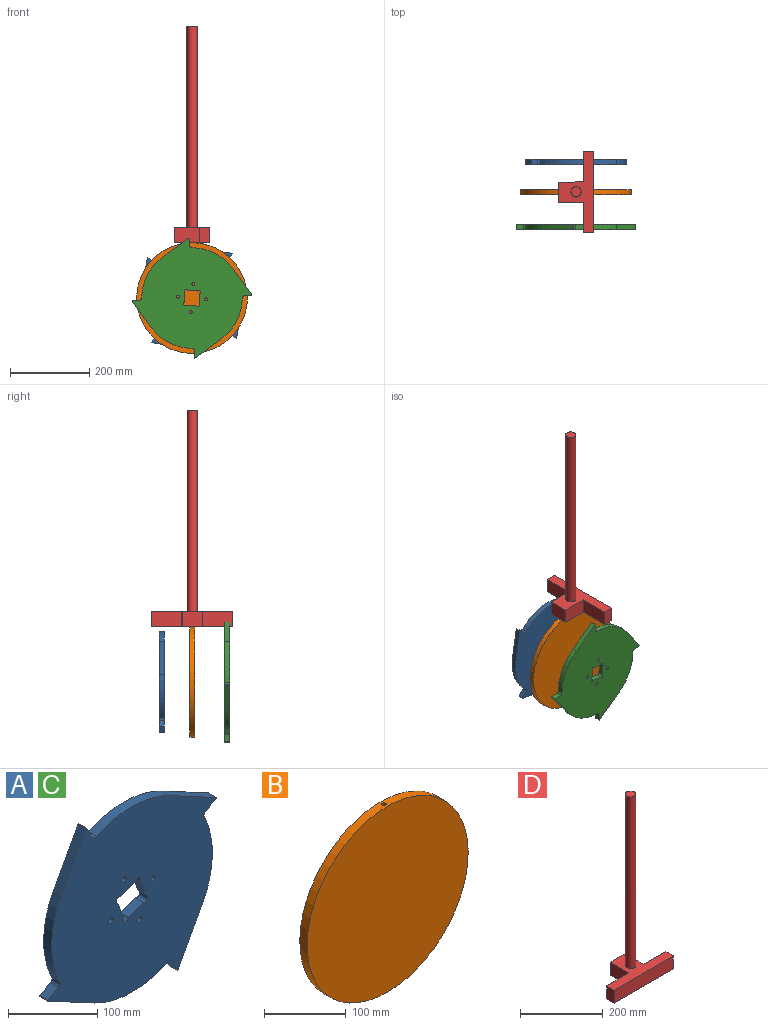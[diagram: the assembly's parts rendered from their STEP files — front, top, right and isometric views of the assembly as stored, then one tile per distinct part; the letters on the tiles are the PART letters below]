
ASSEMBLY  parts=4 mates=3
PART A: 34 faces, bbox 266.9x12.7x266.9 mm
  f0: plane 266.87x266.87mm, normal (0,-1,0), area 51514.2mm2, adj f2,f3,f4,f5,f6,f7,f8,f9
  f1: plane 266.87x266.87mm, normal (0,1,0), area 51514.2mm2, adj f2,f3,f4,f5,f6,f7,f8,f9
  f2: cylinder r=127mm len=115.76mm, axis (0,1,0), area 1526.8mm2, adj f0,f1,f13,f26
  f3: plane 16.74x12.7mm, normal (-0.47,0,0.88), area 241.3mm2, adj f0,f1,f26,f30
  f4: plane 72.98x39.17mm, normal (-0.47,0,-0.88), area 1051.8mm2, adj f0,f1,f5,f30
  f5: cylinder r=127mm len=115.76mm, axis (0,1,0), area 1526.8mm2, adj f0,f1,f4,f27
  f6: plane 16.74x12.7mm, normal (-0.88,0,-0.47), area 241.3mm2, adj f0,f1,f27,f31
  f7: plane 72.98x39.17mm, normal (0.88,0,-0.47), area 1051.8mm2, adj f0,f1,f8,f31
  f8: cylinder r=127mm len=115.76mm, axis (0,1,0), area 1526.8mm2, adj f0,f1,f7,f28
  f9: plane 16.74x12.7mm, normal (0.47,0,-0.88), area 241.3mm2, adj f0,f1,f28,f32
  f10: plane 72.98x39.17mm, normal (0.47,0,0.88), area 1051.8mm2, adj f0,f1,f11,f32
  f11: cylinder r=127mm len=115.76mm, axis (0,1,0), area 1526.8mm2, adj f0,f1,f10,f29
  f12: plane 16.74x12.7mm, normal (0.88,0,0.47), area 241.3mm2, adj f0,f1,f29,f33
  f13: plane 72.98x39.17mm, normal (-0.88,0,0.47), area 1051.8mm2, adj f0,f1,f2,f33
  f14: cylinder r=3.81mm len=12.7mm, axis (0,-1,0), area 304mm2, adj f0,f1
  f15: cylinder r=3.81mm len=12.7mm, axis (0,-1,0), area 304mm2, adj f0,f1
  f16: cylinder r=3.81mm len=12.7mm, axis (0,-1,0), area 304mm2, adj f0,f1
  f17: cylinder r=4.49mm len=12.7mm, axis (0,-1,0), area 179.1mm2, adj f0,f1,f18,f24
  f18: plane 23.87x12.7mm, normal (0.94,0,0.34), area 322.6mm2, adj f0,f1,f17,f19
  f19: cylinder r=4.49mm len=12.7mm, axis (0,-1,0), area 179.1mm2, adj f0,f1,f18,f20
  f20: plane 23.87x12.7mm, normal (-0.34,0,0.94), area 322.6mm2, adj f0,f1,f19,f21
  f21: cylinder r=4.49mm len=12.7mm, axis (0,-1,0), area 179.1mm2, adj f0,f1,f20,f22
  f22: plane 23.87x12.7mm, normal (-0.94,0,-0.34), area 322.6mm2, adj f0,f1,f21,f23
  f23: cylinder r=4.49mm len=12.7mm, axis (0,-1,0), area 179.1mm2, adj f0,f1,f22,f24
  f24: plane 23.87x12.7mm, normal (0.34,0,-0.94), area 322.6mm2, adj f0,f1,f17,f23
  f25: cylinder r=3.81mm len=12.7mm, axis (0,-1,0), area 304mm2, adj f0,f1
  f26: cylinder r=5.08mm len=12.7mm, axis (0,1,0), area 98.9mm2, adj f0,f1,f2,f3
  f27: cylinder r=5.08mm len=12.7mm, axis (0,1,0), area 98.9mm2, adj f0,f1,f5,f6
  f28: cylinder r=5.08mm len=12.7mm, axis (0,1,0), area 98.9mm2, adj f0,f1,f8,f9
  f29: cylinder r=5.08mm len=12.7mm, axis (0,1,0), area 98.9mm2, adj f0,f1,f11,f12
  f30: cylinder r=0.76mm len=12.7mm, axis (0,1,0), area 20.9mm2, adj f0,f1,f3,f4
  f31: cylinder r=0.76mm len=12.7mm, axis (0,1,0), area 20.9mm2, adj f0,f1,f6,f7
  f32: cylinder r=0.76mm len=12.7mm, axis (0,-1,0), area 20.9mm2, adj f0,f1,f9,f10
  f33: cylinder r=0.76mm len=12.7mm, axis (0,1,0), area 20.9mm2, adj f0,f1,f12,f13
PART B: 4 faces, bbox 279.4x12.7x279.4 mm
  f0: cylinder r=139.7mm len=279.4mm, axis (0,1,0), area 11106.9mm2, adj f1,f2,f3
  f1: plane 279.4x279.4mm, normal (0,-1,0), area 61311.6mm2, adj f0
  f2: plane 279.4x279.4mm, normal (0,1,0), area 61311.6mm2, adj f0
  f3: cylinder r=2.54mm len=279.4mm, axis (0,0,-1), area 4458.7mm2, adj f0
PART C: same geometry as A
PART D: 12 faces, bbox 203.2x88.9x546.1 mm
  f0: plane 50.8x38.1mm, normal (0,1,0), area 1935.5mm2, adj f6,f7,f8,f11
  f1: plane 38.1x25.4mm, normal (1,0,0), area 967.7mm2, adj f5,f6,f7,f9
  f2: plane 38.1x25.4mm, normal (-1,0,0), area 967.7mm2, adj f5,f6,f7,f10
  f3: cylinder r=12.7mm len=508mm, axis (0,0,-1), area 40536.6mm2, adj f4,f7
  f4: plane 25.4x25.4mm, normal (0,0,1), area 506.7mm2, adj f3
  f5: plane 203.2x38.1mm, normal (0,-1,0), area 7741.9mm2, adj f1,f2,f6,f7
  f6: plane 203.2x88.9mm, normal (0,0,-1), area 8387.1mm2, adj f0,f1,f2,f5,f8,f9,f10,f11
  f7: plane 203.2x88.9mm, normal (0,0,1), area 7880.4mm2, adj f0,f1,f2,f3,f5,f8,f9,f10
  f8: plane 63.5x38.1mm, normal (1,0,0), area 2419.4mm2, adj f0,f6,f7,f9
  f9: plane 76.2x38.1mm, normal (0,1,0), area 2903.2mm2, adj f1,f6,f7,f8
  f10: plane 76.2x38.1mm, normal (0,1,0), area 2903.2mm2, adj f2,f6,f7,f11
  f11: plane 63.5x38.1mm, normal (-1,0,0), area 2419.4mm2, adj f0,f6,f7,f10
PLACE A rot(axis=(0,-1,0),19.3deg) t=(258.99,82.55,-124.51)mm
PLACE B t=(-233.82,6.35,-203.2)mm
PLACE C rot(axis=(0,-1,0),64.3deg) t=(271.18,-82.55,95.09)mm
PLACE D rot(axis=(0,0,1),90.3deg) t=(0,6.35,179.48)mm
MATE revolute B.f3 <-> D.f3  axis (0,0,-1) through (0,6.35,141.38)mm
MATE revolute C.f2 <-> B.f0  axis (0,1,0) through (0,-76.2,0)mm
MATE fastened A.f2 <-> C.f2  axis (0,-1,0) through (0,76.2,0)mm
